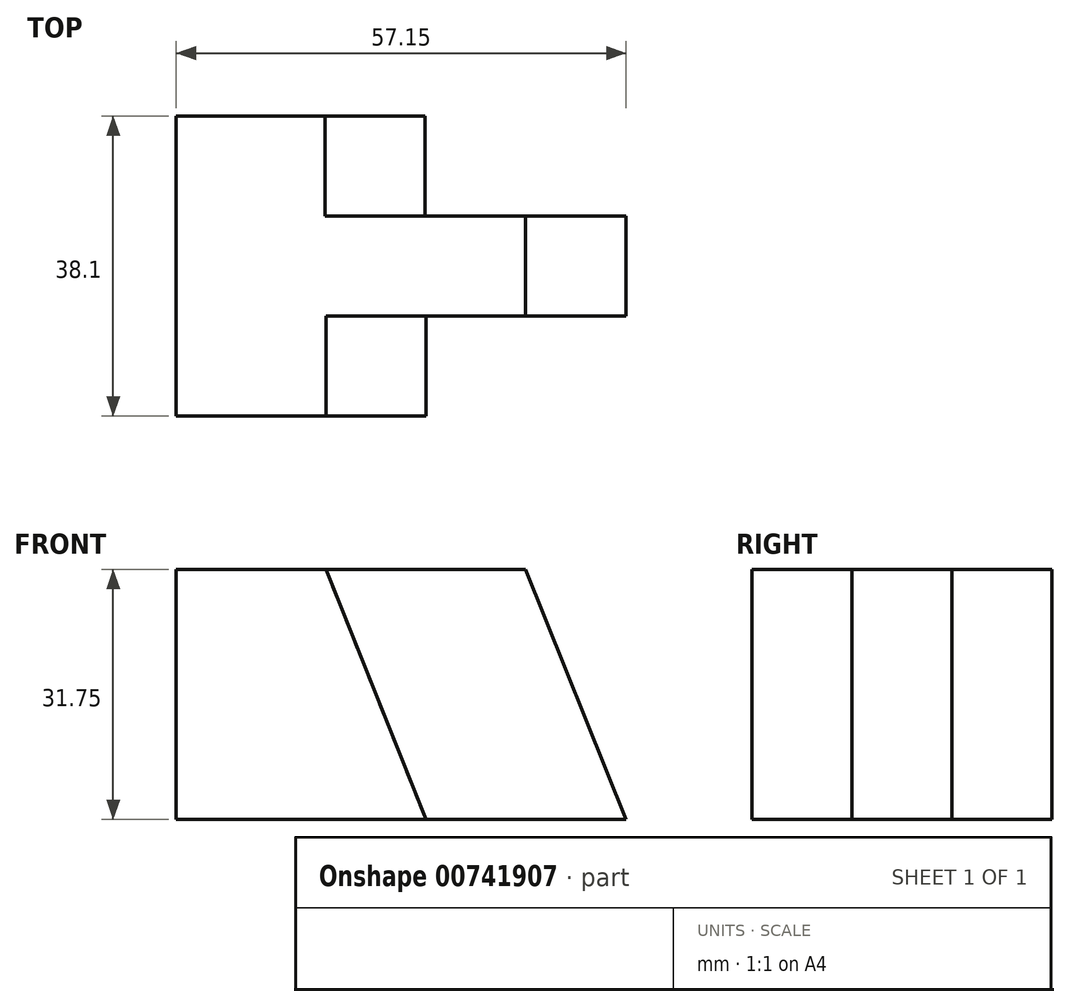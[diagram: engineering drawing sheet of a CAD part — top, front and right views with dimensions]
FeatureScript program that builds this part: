
annotation { "Feature Type Name" : "Feature", "Feature Type Description" : "" }
export const myFeature = defineFeature(function(context is Context, id is Id, definition is map)
    precondition{}
    {
        {
            var Q0;
            Q0=qCreatedBy(makeId("Top.planeOp"),FACE);
            var sketch = newSketch(context, id + "F0", { "sketchPlane" : qUnion([Q0])});
            skLineSegment(sketch, "E0", {"start": v(0, 0) * mm, "end": v(0, -38.1) * mm});
            skLineSegment(sketch, "E1", {"start": v(0, -38.1) * mm, "end": v(31.75, -38.1) * mm});
            skLineSegment(sketch, "E2", {"start": v(31.75, -38.1) * mm, "end": v(31.75, -25.4) * mm});
            skLineSegment(sketch, "E3", {"start": v(31.75, -25.4) * mm, "end": v(57.15, -25.4) * mm});
            skLineSegment(sketch, "E4", {"start": v(57.15, -25.4) * mm, "end": v(57.15, -12.7) * mm});
            skLineSegment(sketch, "E5", {"start": v(57.15, -12.7) * mm, "end": v(31.6, -12.7) * mm});
            skLineSegment(sketch, "E6", {"start": v(31.6, -12.7) * mm, "end": v(31.6, 0) * mm});
            skLineSegment(sketch, "E7", {"start": v(31.6, 0) * mm, "end": v(-0.15, 0) * mm});
            skLineSegment(sketch, "E8", {"start": v(-0.15, 0) * mm, "end": v(0, -38.1) * mm});
            skSolve(sketch);
        }
        {
            var Q0;
            {var subQ0=sQuery(id+"F0.wireOp",EDGE,"E1");Q0=makeQuery(id+"F0.imprint","IMPRINT",FACE,{"disambiguationData":[TD([[makeQuery(id+"F0.imprint","IMPRINT",EDGE,{"derivedFrom":subQ0}),1.0]])]});}
            extrude(context, id + "F1", {"entities" : qUnion([Q0]), "depth" : 31.75 * mm, "offsetDistance" : 25.4 * mm});
        }
        {
            var Q0;
            Q0=makeQuery(id+"F1.opExtrude","SWEPT_FACE",FACE,{"disambiguationData":[OSD([sQuery(id+"F0.wireOp",EDGE,"E1")])]});
            var sketch = newSketch(context, id + "F2", { "sketchPlane" : qUnion([Q0])});
            skLineSegment(sketch, "E9", {"start": v(31.75, 31.75) * mm, "end": v(19.05, 31.75) * mm});
            skLineSegment(sketch, "E10", {"start": v(19.05, 31.75) * mm, "end": v(31.75, 0) * mm});
            skSolve(sketch);
        }
        {
            var Q0;
            Q0=makeQuery(id+"F2.imprint","IMPRINT",FACE,{"disambiguationData":[TD([[makeQuery(id+"F2.imprint","IMPRINT",EDGE,{"derivedFrom":sQuery(id+"F2.wireOp",EDGE,"E9")}),-1.0]])]});
            extrude(context, id + "F3", {"entities" : qUnion([Q0]), "operationType" : NewBodyOperationType.REMOVE, "oppositeDirection" : true, "depth" : 12.7 * mm, "offsetDistance" : 25.4 * mm});
        }
        {
            var Q0;
            Q0=makeQuery(id+"F1.opExtrude","SWEPT_FACE",FACE,{"disambiguationData":[OSD([sQuery(id+"F0.wireOp",EDGE,"E7")])]});
            var sketch = newSketch(context, id + "F4", { "sketchPlane" : qUnion([Q0])});
            skLineSegment(sketch, "E11", {"start": v(-31.6, 31.75) * mm, "end": v(-18.9, 31.75) * mm});
            skLineSegment(sketch, "E12", {"start": v(-18.9, 31.75) * mm, "end": v(-31.6, 0) * mm});
            skSolve(sketch);
        }
        {
            var Q0;
            Q0=makeQuery(id+"F4.imprint","IMPRINT",FACE,{"disambiguationData":[TD([[makeQuery(id+"F4.imprint","IMPRINT",EDGE,{"derivedFrom":sQuery(id+"F4.wireOp",EDGE,"E11")}),-1.0]])]});
            extrude(context, id + "F5", {"entities" : qUnion([Q0]), "operationType" : NewBodyOperationType.REMOVE, "oppositeDirection" : true, "depth" : 12.7 * mm, "offsetDistance" : 25.4 * mm});
        }
        {
            var Q0;
            Q0=makeQuery(id+"F1.opExtrude","SWEPT_FACE",FACE,{"disambiguationData":[OSD([sQuery(id+"F0.wireOp",EDGE,"E5")])]});
            var sketch = newSketch(context, id + "F6", { "sketchPlane" : qUnion([Q0])});
            skLineSegment(sketch, "E13", {"start": v(-57.15, 31.75) * mm, "end": v(-44.37, 31.75) * mm});
            skLineSegment(sketch, "E14", {"start": v(-44.37, 31.75) * mm, "end": v(-57.15, 0) * mm});
            skLineSegment(sketch, "E15", {"start": v(-57.15, 0) * mm, "end": v(-57.15, 31.75) * mm});
            skSolve(sketch);
        }
        {
            var Q0;
            Q0=makeQuery(id+"F6.imprint","IMPRINT",FACE,{"disambiguationData":[TD([[makeQuery(id+"F6.imprint","IMPRINT",EDGE,{"derivedFrom":sQuery(id+"F6.wireOp",EDGE,"E13")}),-1.0]])]});
            extrude(context, id + "F7", {"entities" : qUnion([Q0]), "operationType" : NewBodyOperationType.REMOVE, "endBound" : BoundingType.THROUGH_ALL, "oppositeDirection" : true, "depth" : 25.4 * mm, "offsetDistance" : 25.4 * mm});
        }
    });
